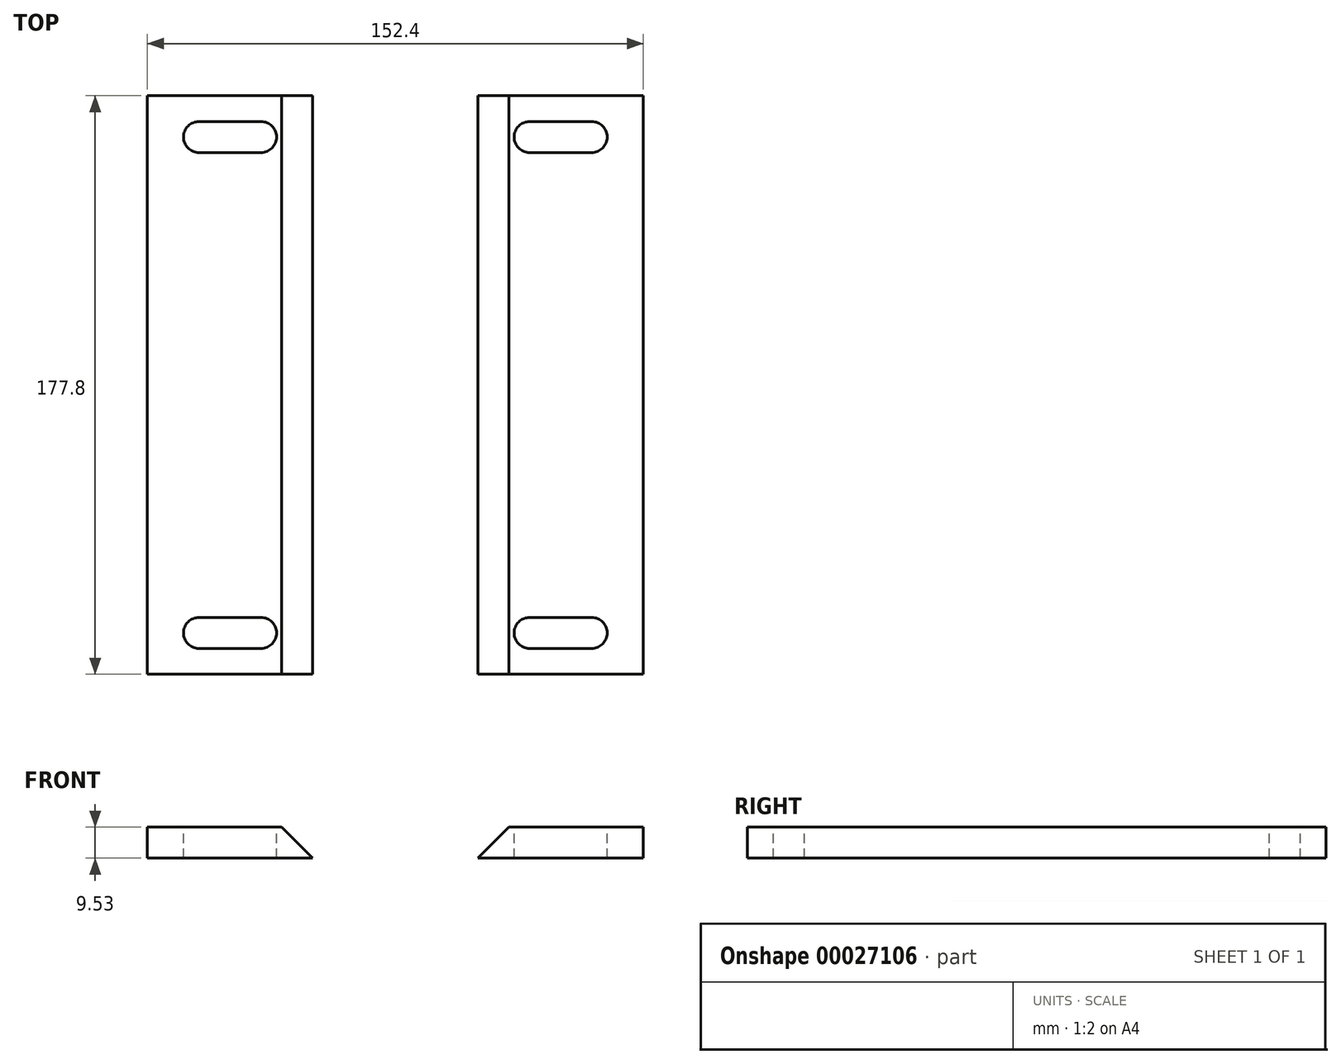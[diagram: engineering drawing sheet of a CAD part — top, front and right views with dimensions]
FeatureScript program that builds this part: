
annotation { "Feature Type Name" : "Feature", "Feature Type Description" : "" }
export const myFeature = defineFeature(function(context is Context, id is Id, definition is map)
    precondition{}
    {
        {
            var Q0;
            Q0=qCreatedBy(makeId("Top.planeOp"),FACE);
            var sketch = newSketch(context, id + "F0", { "sketchPlane" : qUnion([Q0])});
            skLineSegment(sketch, "E0.bottom", {"start": v(0, 121.87) * mm, "end": v(-50.8, 121.87) * mm});
            skLineSegment(sketch, "E0.top", {"start": v(0, -55.93) * mm, "end": v(-50.8, -55.93) * mm});
            skLineSegment(sketch, "E0.left", {"start": v(0, 121.87) * mm, "end": v(0, -55.93) * mm});
            skLineSegment(sketch, "E0.right", {"start": v(-50.8, 121.87) * mm, "end": v(-50.8, -55.93) * mm});
            skSolve(sketch);
        }
        {
            var Q0;
            Q0=makeQuery(id+"F0.imprint","IMPRINT",FACE,{"disambiguationData":[TD([[makeQuery(id+"F0.imprint","IMPRINT",EDGE,{"derivedFrom":sQuery(id+"F0.wireOp",EDGE,"E0.bottom")}),1.0]])]});
            extrude(context, id + "F1", {"entities" : qUnion([Q0]), "depth" : 9.52 * mm});
        }
        {
            var Q0;
            Q0=makeQuery(id+"F1.opExtrude","CAP_FACE",FACE,{"disambiguationData":[OSD([sQuery(id+"F0.wireOp",EDGE,"E0.bottom"),sQuery(id+"F0.wireOp",EDGE,"E0.top"),sQuery(id+"F0.wireOp",EDGE,"E0.left"),sQuery(id+"F0.wireOp",EDGE,"E0.right")])],"isStart":false});
            var sketch = newSketch(context, id + "F2", { "sketchPlane" : qUnion([Q0])});
            skLineSegment(sketch, "E1", {"start": v(-25.4, -55.93) * mm, "end": v(-25.4, 121.87) * mm, "construction": true});
            skLineSegment(sketch, "E2", {"start": v(-50.8, 32.97) * mm, "end": v(0, 32.97) * mm, "construction": true});
            skPoint(sketch, "E3", {"position": v(-25.4, -43.23) * mm});
            skPoint(sketch, "E4.MirrorP", {"position": v(-25.4, 109.17) * mm});
            skLineSegment(sketch, "E5.rect.bottom", {"start": v(-15.87, -38.47) * mm, "end": v(-34.92, -38.47) * mm});
            skLineSegment(sketch, "E5.rect.top", {"start": v(-15.87, -48) * mm, "end": v(-34.92, -48) * mm});
            skPoint(sketch, "E6.visualSharp", {"position": v(-34.92, -48) * mm});
            skLineSegment(sketch, "E6.filletArc", {"start": v(-34.92, -48) * mm, "end": v(-34.92, -48) * mm});
            skArc(sketch, "E7", {"start": v(-34.92, -38.47) * mm, "mid": v(-39.69, -43.23) * mm, "end": v(-34.92, -48) * mm});
            skArc(sketch, "E8", {"start": v(-15.87, -48) * mm, "mid": v(-11.11, -43.23) * mm, "end": v(-15.87, -38.47) * mm});
            skLineSegment(sketch, "E9.MirrorCS", {"start": v(-15.87, 104.4) * mm, "end": v(-34.92, 104.4) * mm});
            skArc(sketch, "E10.MirrorCS", {"start": v(-34.92, 104.4) * mm, "mid": v(-39.69, 109.17) * mm, "end": v(-34.92, 113.93) * mm});
            skLineSegment(sketch, "E11.MirrorCS", {"start": v(-15.87, 113.93) * mm, "end": v(-34.92, 113.93) * mm});
            skArc(sketch, "E12.MirrorCS", {"start": v(-15.87, 113.93) * mm, "mid": v(-11.11, 109.17) * mm, "end": v(-15.87, 104.4) * mm});
            skSolve(sketch);
        }
        {
            var Q0;
            Q0=makeQuery(id+"F1.opExtrude","CAP_EDGE",EDGE,{"disambiguationData":[OSD([sQuery(id+"F0.wireOp",EDGE,"E0.left")])],"isStart":false});
            chamfer(context, id + "F3", {"entities" : qUnion([Q0]), "width" : 9.52 * mm, "tangentPropagation" : true});
        }
        {
            var Q0;
            Q0=makeQuery(id+"F2.imprint","IMPRINT",FACE,{"disambiguationData":[TD([[makeQuery(id+"F2.imprint","IMPRINT",EDGE,{"derivedFrom":sQuery(id+"F2.wireOp",EDGE,"E5.rect.bottom")}),1.0]])]});
            var Q1;
            Q1=makeQuery(id+"F2.imprint","IMPRINT",FACE,{"disambiguationData":[TD([[makeQuery(id+"F2.imprint","IMPRINT",EDGE,{"derivedFrom":sQuery(id+"F2.wireOp",EDGE,"E9.MirrorCS")}),-1.0]])]});
            extrude(context, id + "F4", {"entities" : qUnion([Q0, Q1]), "operationType" : NewBodyOperationType.REMOVE, "oppositeDirection" : true, "depth" : 9.52 * mm});
        }
        {
            var Q0;
            Q0=makeQuery(id+"F1.opExtrude","SWEPT_BODY",BODY,{"disambiguationData":[OSD([sQuery(id+"F0.wireOp",EDGE,"E0.bottom"),sQuery(id+"F0.wireOp",EDGE,"E0.top"),sQuery(id+"F0.wireOp",EDGE,"E0.left"),sQuery(id+"F0.wireOp",EDGE,"E0.right")])]});
            var Q1;
            Q1=qCreatedBy(makeId("Right.planeOp"),FACE);
            mirror(context, id + "F5", {"entities" : qUnion([Q0]), "mirrorPlane" : qUnion([Q1])});
        }
        {
            var Q0;
            Q0=makeQuery(id+"F1.opExtrude","SWEPT_BODY",BODY,{"disambiguationData":[OSD([sQuery(id+"F0.wireOp",EDGE,"E0.bottom"),sQuery(id+"F0.wireOp",EDGE,"E0.top"),sQuery(id+"F0.wireOp",EDGE,"E0.left"),sQuery(id+"F0.wireOp",EDGE,"E0.right")])]});
            var Q1;
            Q1=qCreatedBy(makeId("Right.planeOp"),FACE);
            transform(context, id + "F6", {"entities" : qUnion([Q0]), "transformType" : TransformType.TRANSLATION_DISTANCE, "transformDirection" : qUnion([Q1]), "distance" : 25.4 * mm, "oppositeDirection" : true, "makeCopy" : false});
        }
        {
            var Q0;
            Q0=makeQuery(id+"F5.opPattern","COPY",BODY,{"derivedFrom":makeQuery(id+"F1.opExtrude","SWEPT_BODY",BODY,{"disambiguationData":[OSD([sQuery(id+"F0.wireOp",EDGE,"E0.bottom"),sQuery(id+"F0.wireOp",EDGE,"E0.top"),sQuery(id+"F0.wireOp",EDGE,"E0.left"),sQuery(id+"F0.wireOp",EDGE,"E0.right")])]}),"instanceName":"1"});
            var Q1;
            Q1=qCreatedBy(makeId("Right.planeOp"),FACE);
            transform(context, id + "F7", {"entities" : qUnion([Q0]), "transformType" : TransformType.TRANSLATION_DISTANCE, "transformDirection" : qUnion([Q1]), "distance" : 25.4 * mm, "makeCopy" : false});
        }
    });
